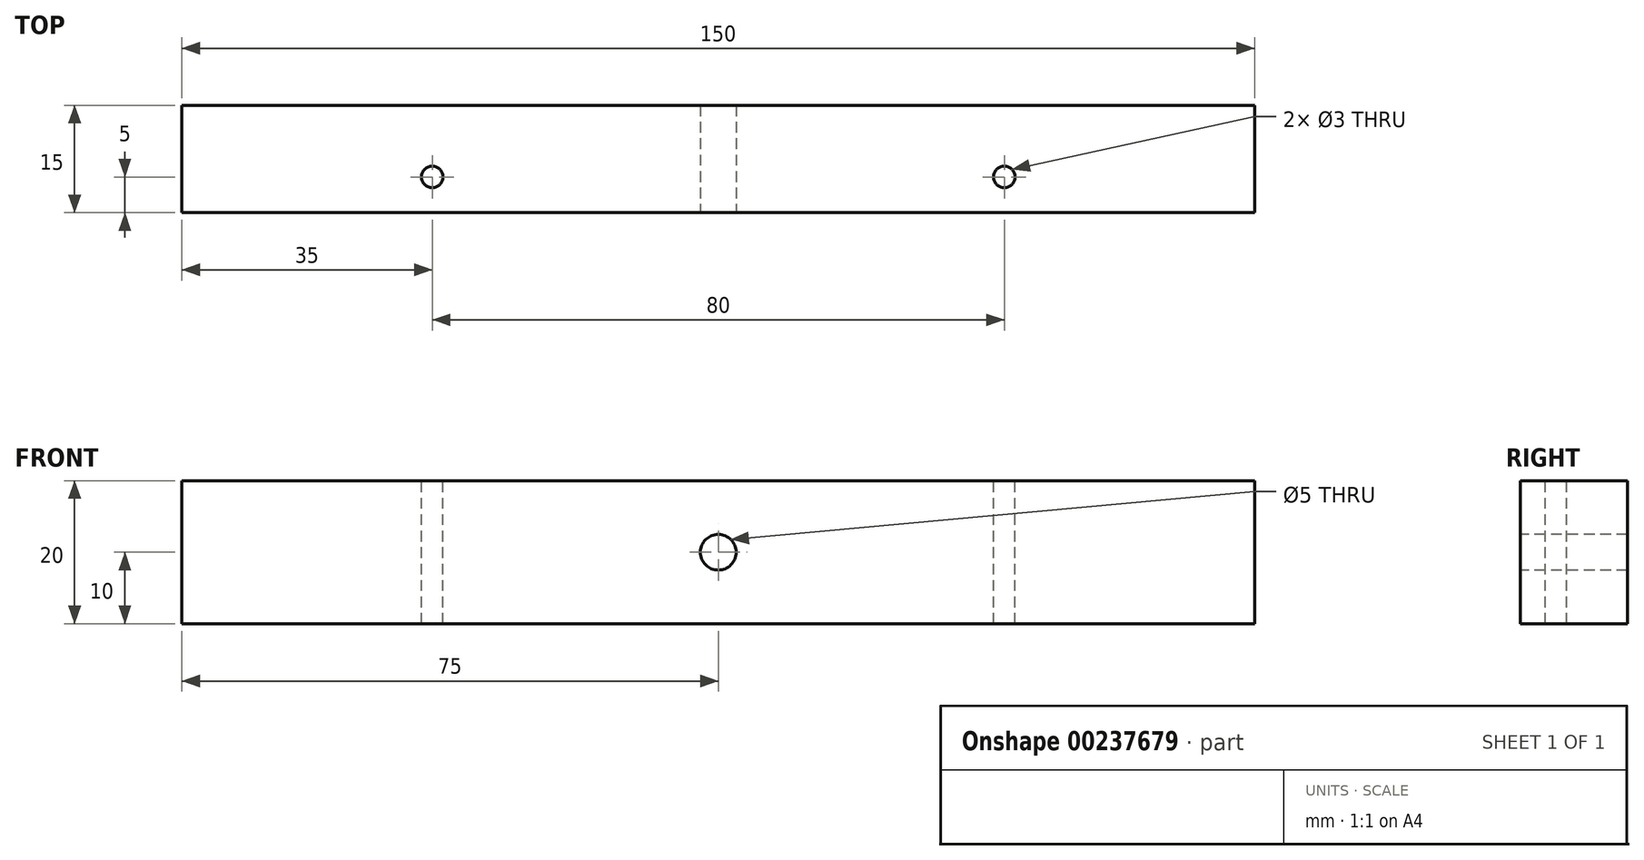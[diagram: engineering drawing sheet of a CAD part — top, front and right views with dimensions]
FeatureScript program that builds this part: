
annotation { "Feature Type Name" : "Feature", "Feature Type Description" : "" }
export const myFeature = defineFeature(function(context is Context, id is Id, definition is map)
    precondition{}
    {
        {
            var Q0;
            Q0=qCreatedBy(makeId("Top.planeOp"),FACE);
            var sketch = newSketch(context, id + "F0", { "sketchPlane" : qUnion([Q0])});
            skLineSegment(sketch, "E0", {"start": v(75, 0) * mm, "end": v(75, 10) * mm});
            skLineSegment(sketch, "E1", {"start": v(75, 10) * mm, "end": v(-75, 10) * mm});
            skLineSegment(sketch, "E2", {"start": v(-75, 10) * mm, "end": v(-75, -10) * mm});
            skLineSegment(sketch, "E3", {"start": v(-75, -10) * mm, "end": v(75, -10) * mm});
            skLineSegment(sketch, "E4", {"start": v(75, -10) * mm, "end": v(75, 0) * mm});
            skSolve(sketch);
        }
        {
            var Q0;
            Q0 = qSketchRegion(id + "F0", true);
            extrude(context, id + "F1", {"entities" : qUnion([Q0]), "depth" : 20 * mm});
        }
        {
            var Q0;
            Q0=makeQuery(id+"F1.opExtrude","CAP_FACE",FACE,{"disambiguationData":[OSD([sQuery(id+"F0.wireOp",EDGE,"E0"),sQuery(id+"F0.wireOp",EDGE,"E1"),sQuery(id+"F0.wireOp",EDGE,"E2"),sQuery(id+"F0.wireOp",EDGE,"E3"),sQuery(id+"F0.wireOp",EDGE,"E4")])],"isStart":false});
            var sketch = newSketch(context, id + "F2", { "sketchPlane" : qUnion([Q0])});
            skCircle(sketch, "E5", {"center": v(-40, 0) * mm, "radius": 1.5 * mm});
            skCircle(sketch, "E6", {"center": v(40, 0) * mm, "radius": 1.5 * mm});
            skSolve(sketch);
        }
        {
            var Q0;
            Q0 = qSketchRegion(id + "F2", true);
            extrude(context, id + "F3", {"entities" : qUnion([Q0]), "operationType" : NewBodyOperationType.REMOVE, "oppositeDirection" : true, "depth" : 25 * mm});
        }
        {
            var Q0;
            Q0=makeQuery(id+"F1.opExtrude","SWEPT_FACE",FACE,{"disambiguationData":[OSD([sQuery(id+"F0.wireOp",EDGE,"E3")])]});
            var sketch = newSketch(context, id + "F4", { "sketchPlane" : qUnion([Q0])});
            skCircle(sketch, "E7", {"center": v(0, 10) * mm, "radius": 2.5 * mm});
            skSolve(sketch);
        }
        {
            var Q0;
            Q0 = qSketchRegion(id + "F4", true);
            extrude(context, id + "F5", {"entities" : qUnion([Q0]), "operationType" : NewBodyOperationType.REMOVE, "oppositeDirection" : true, "depth" : 25 * mm});
        }
        {
            var Q0;
            Q0=makeQuery(id+"F1.opExtrude","SWEPT_FACE",FACE,{"disambiguationData":[OSD([sQuery(id+"F0.wireOp",EDGE,"E3")])]});
            extrude(context, id + "F6", {"entities" : qUnion([Q0]), "operationType" : NewBodyOperationType.REMOVE, "oppositeDirection" : true, "depth" : 5 * mm});
        }
    });
